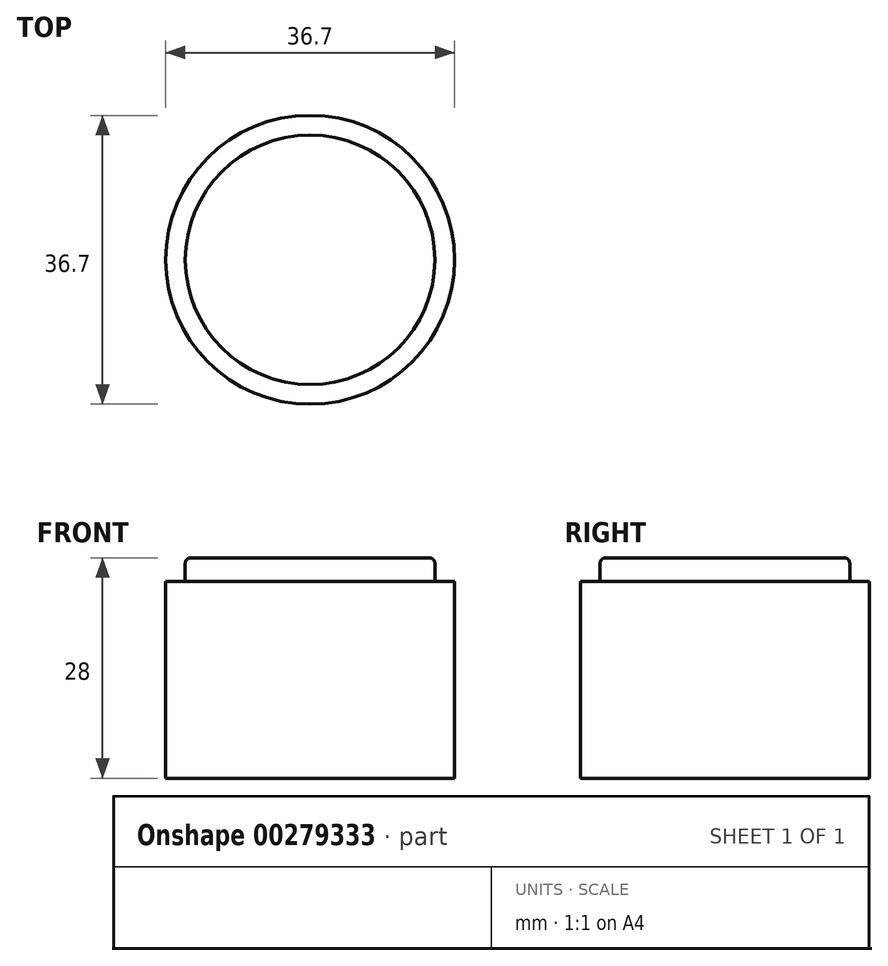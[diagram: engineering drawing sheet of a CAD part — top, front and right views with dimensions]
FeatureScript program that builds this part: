
annotation { "Feature Type Name" : "Feature", "Feature Type Description" : "" }
export const myFeature = defineFeature(function(context is Context, id is Id, definition is map)
    precondition{}
    {
        {
            var Q0;
            Q0=qCreatedBy(makeId("Top.planeOp"),FACE);
            var sketch = newSketch(context, id + "F0", { "sketchPlane" : qUnion([Q0])});
            skCircle(sketch, "E0", {"center": v(0, 0) * mm, "radius": 18.35 * mm});
            skSolve(sketch);
        }
        {
            var Q0;
            Q0=makeQuery(id+"F0.imprint","IMPRINT",FACE,{"disambiguationData":[TD([[makeQuery(id+"F0.imprint","IMPRINT",EDGE,{"derivedFrom":sQuery(id+"F0.wireOp",EDGE,"E0")}),1.0]])]});
            var Q1;
            Q1=sQuery(id+"F0.wireOp",EDGE,"E0");
            extrude(context, id + "F1", {"entities" : qUnion([Q0]), "surfaceEntities" : qUnion([Q1]), "depth" : 25 * mm});
        }
        {
            var Q0;
            Q0=makeQuery(id+"F1.opExtrude","CAP_FACE",FACE,{"disambiguationData":[OSD([sQuery(id+"F0.wireOp",EDGE,"E0")])],"isStart":false});
            var sketch = newSketch(context, id + "F2", { "sketchPlane" : qUnion([Q0])});
            skCircle(sketch, "E1", {"center": v(0, 0) * mm, "radius": 15.85 * mm});
            skSolve(sketch);
        }
        {
            var Q0;
            Q0 = qSketchRegion(id + "F2", true);
            extrude(context, id + "F3", {"entities" : qUnion([Q0]), "operationType" : NewBodyOperationType.ADD, "depth" : 3 * mm});
        }
        {
            var Q0;
            Q0=makeQuery(id+"F3.opExtrude","CAP_EDGE",EDGE,{"disambiguationData":[OSD([sQuery(id+"F2.wireOp",EDGE,"E1")])],"isStart":false});
            fillet(context, id + "F4", {"entities" : qUnion([Q0]), "radius" : .7 * mm, "tangentPropagation" : true, "allowEdgeOverflow" : false});
        }
    });
